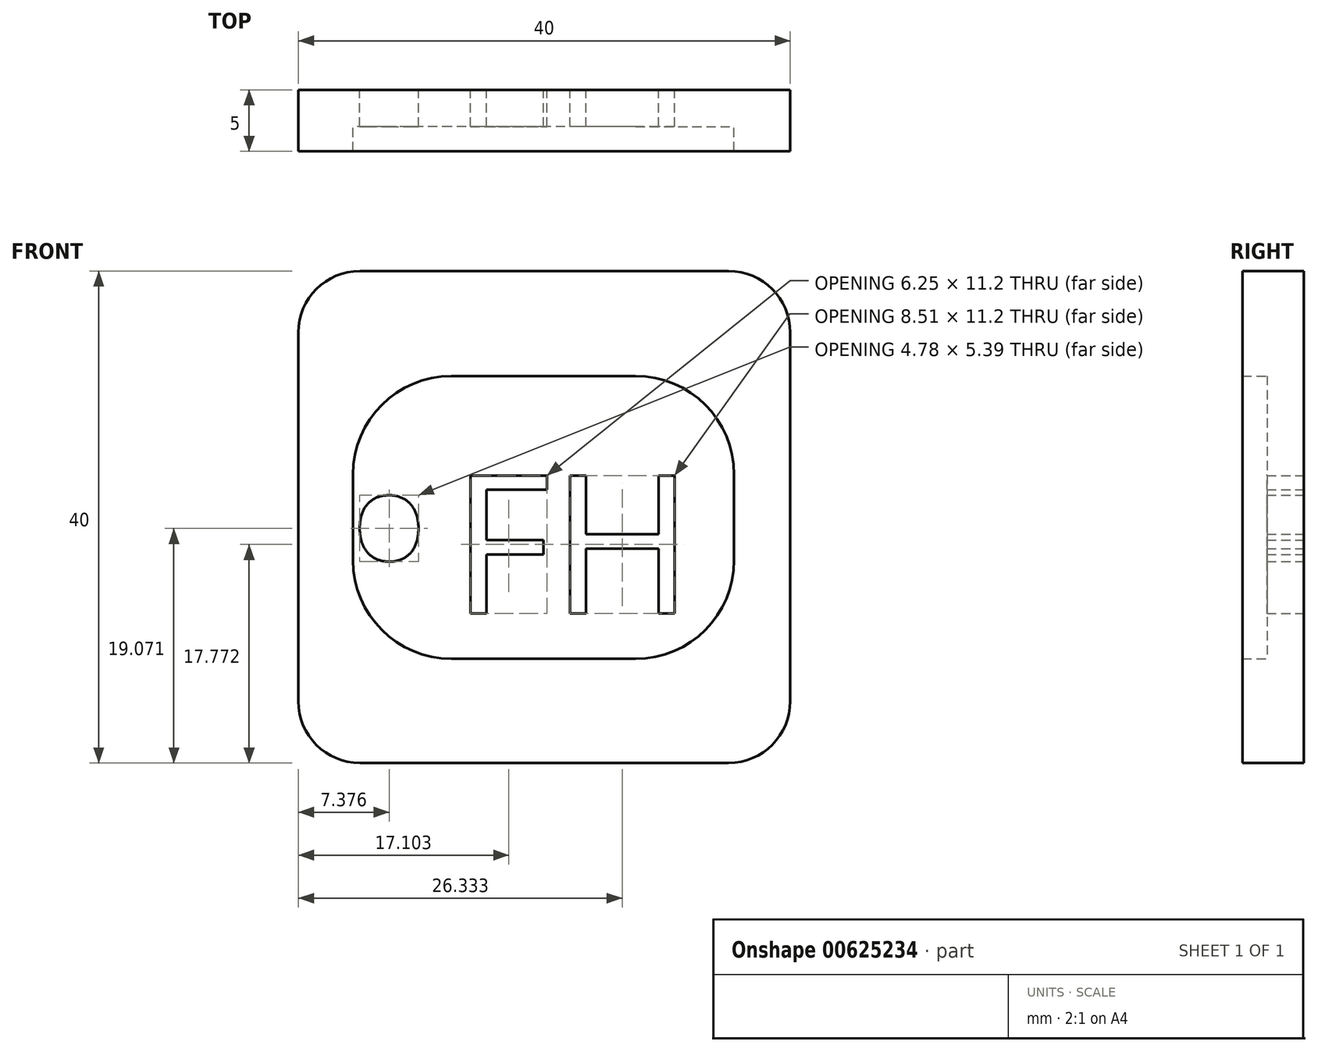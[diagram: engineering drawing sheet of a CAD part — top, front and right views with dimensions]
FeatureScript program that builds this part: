
annotation { "Feature Type Name" : "Feature", "Feature Type Description" : "" }
export const myFeature = defineFeature(function(context is Context, id is Id, definition is map)
    precondition{}
    {
        {
            var Q0;
            Q0=qCreatedBy(makeId("Front.planeOp"),FACE);
            var sketch = newSketch(context, id + "F0", { "sketchPlane" : qUnion([Q0])});
            skLineSegment(sketch, "E0.bottom", {"start": v(-8, 0) * mm, "end": v(-23, 0) * mm});
            skLineSegment(sketch, "E0.top", {"start": v(-8, 23) * mm, "end": v(-23, 23) * mm});
            skLineSegment(sketch, "E0.left", {"start": v(0, 8) * mm, "end": v(0, 15) * mm});
            skLineSegment(sketch, "E0.right", {"start": v(-31, 8) * mm, "end": v(-31, 15) * mm});
            skPoint(sketch, "E1.visualSharp", {"position": v(-31, 23) * mm});
            skArc(sketch, "E1.filletArc", {"start": v(-23, 23) * mm, "mid": v(-28.66, 20.66) * mm, "end": v(-31, 15) * mm});
            skPoint(sketch, "E2.visualSharp", {"position": v(-31, 0) * mm});
            skArc(sketch, "E2.filletArc", {"start": v(-31, 8) * mm, "mid": v(-28.66, 2.34) * mm, "end": v(-23, 0) * mm});
            skPoint(sketch, "E3.visualSharp", {"position": v(0, 23) * mm});
            skArc(sketch, "E3.filletArc", {"start": v(0, 15) * mm, "mid": v(-2.34, 20.66) * mm, "end": v(-8, 23) * mm});
            skPoint(sketch, "E4.visualSharp", {"position": v(0, 0) * mm});
            skArc(sketch, "E4.filletArc", {"start": v(-8, 0) * mm, "mid": v(-2.34, 2.34) * mm, "end": v(0, 8) * mm});
            skText(sketch, "E5", { "text": "FH\n", "fontName": "OpenSans-Regular.ttf"});
            skText(sketch, "E6", { "text": "o", "fontName": "OpenSans-Regular.ttf"});
            skLineSegment(sketch, "E7.bottom", {"start": v(-30.44, 31.53) * mm, "end": v(-0.44, 31.53) * mm});
            skLineSegment(sketch, "E7.top", {"start": v(-30.44, -8.47) * mm, "end": v(-0.44, -8.47) * mm});
            skLineSegment(sketch, "E7.left", {"start": v(-35.44, 26.53) * mm, "end": v(-35.44, -3.47) * mm});
            skLineSegment(sketch, "E7.right", {"start": v(4.56, 26.53) * mm, "end": v(4.56, -3.47) * mm});
            skPoint(sketch, "E8.visualSharp", {"position": v(-35.44, 31.53) * mm});
            skArc(sketch, "E8.filletArc", {"start": v(-30.44, 31.53) * mm, "mid": v(-33.98, 30.07) * mm, "end": v(-35.44, 26.53) * mm});
            skPoint(sketch, "E9.visualSharp", {"position": v(4.56, 31.53) * mm});
            skArc(sketch, "E9.filletArc", {"start": v(4.56, 26.53) * mm, "mid": v(3.1, 30.07) * mm, "end": v(-0.44, 31.53) * mm});
            skPoint(sketch, "E10.visualSharp", {"position": v(4.56, -8.47) * mm});
            skArc(sketch, "E10.filletArc", {"start": v(-0.44, -8.47) * mm, "mid": v(3.1, -7) * mm, "end": v(4.56, -3.47) * mm});
            skPoint(sketch, "E11.visualSharp", {"position": v(-35.44, -8.47) * mm});
            skArc(sketch, "E11.filletArc", {"start": v(-35.44, -3.47) * mm, "mid": v(-33.98, -7) * mm, "end": v(-30.44, -8.47) * mm});
            const initialGuessF0  = {"E5": [-0.023, 0.0037, 1, 0, 0.0113], "E6": [-0.031, 0.008, 1, 0, 0.007]};
            skSetInitialGuess(sketch, initialGuessF0);
            skSolve(sketch);
        }
        {
            var Q0;
            Q0=makeQuery(id+"F0.imprint","IMPRINT",FACE,{"disambiguationData":[TD([[makeQuery(id+"F0.imprint","IMPRINT",EDGE,{"derivedFrom":sQuery(id+"F0.wireOp",EDGE,"E0.bottom")}),-1.0]])]});
            extrude(context, id + "F1", {"entities" : qUnion([Q0]), "depth" : 3 * mm, "offsetDistance" : 25 * mm});
        }
        {
            var Q0;
            Q0 = qSketchRegion(id + "F0", true);
            extrude(context, id + "F2", {"entities" : qUnion([Q0]), "operationType" : NewBodyOperationType.ADD, "depth" : 5 * mm, "offsetDistance" : 25 * mm});
        }
    });
